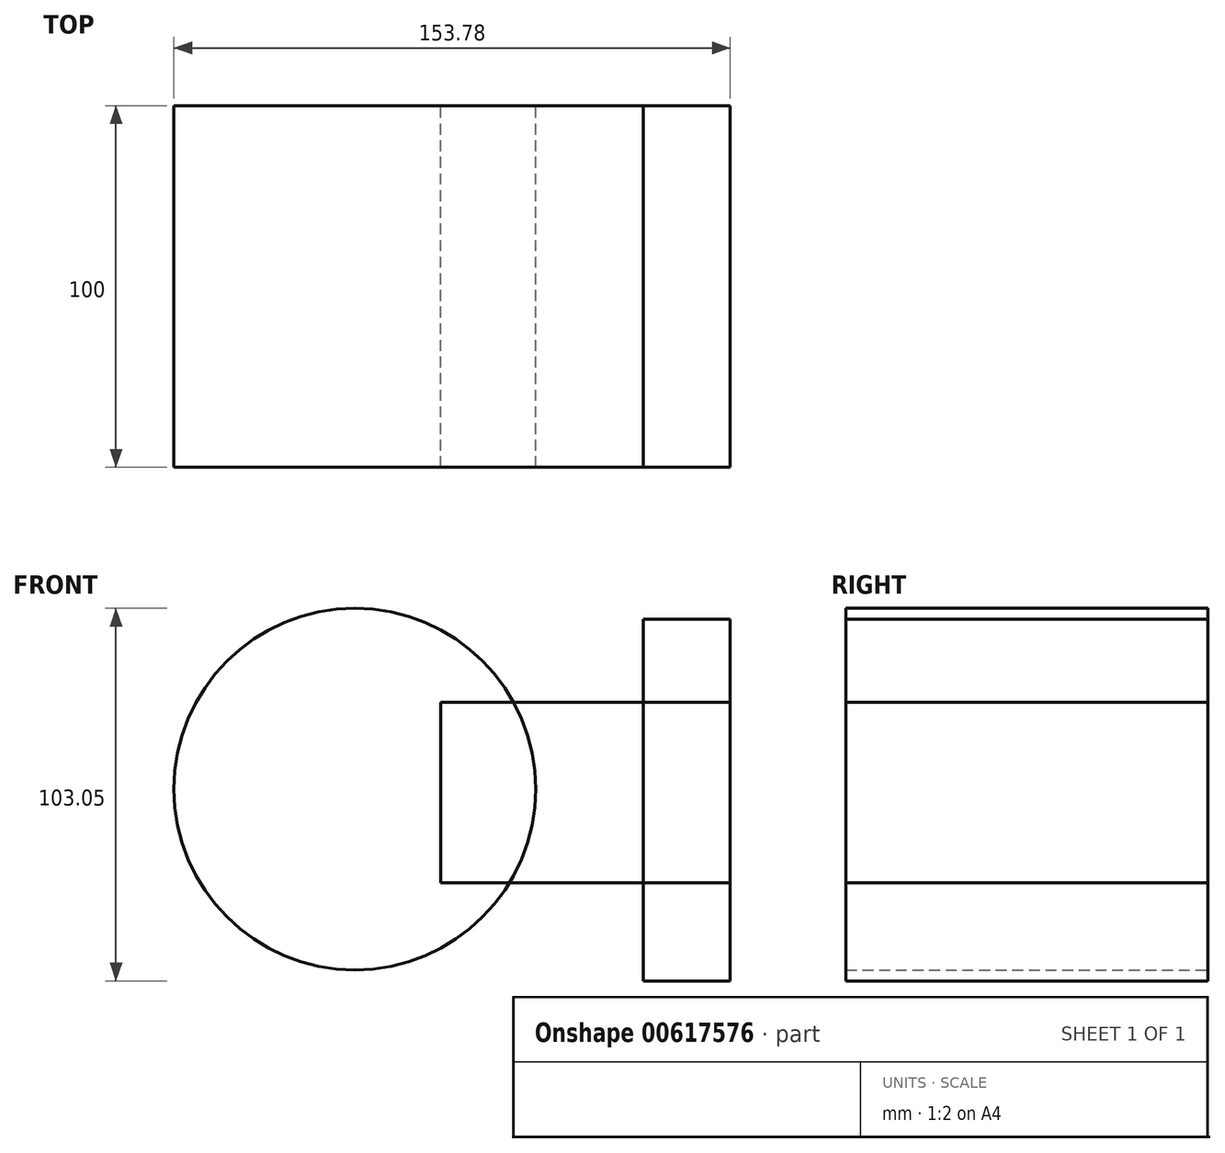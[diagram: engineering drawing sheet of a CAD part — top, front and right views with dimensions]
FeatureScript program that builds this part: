
annotation { "Feature Type Name" : "Feature", "Feature Type Description" : "" }
export const myFeature = defineFeature(function(context is Context, id is Id, definition is map)
    precondition{}
    {
        {
            var Q0;
            Q0=qCreatedBy(makeId("Front.planeOp"),FACE);
            var sketch = newSketch(context, id + "F0", { "sketchPlane" : qUnion([Q0])});
            skCircle(sketch, "E0", {"center": v(-79.77, 0) * mm, "radius": 50 * mm});
            skSolve(sketch);
        }
        {
            var Q0;
            Q0=qCreatedBy(makeId("Front.planeOp"),FACE);
            var sketch = newSketch(context, id + "F1", { "sketchPlane" : qUnion([Q0])});
            skLineSegment(sketch, "E1.bottom", {"start": v(-55.99, 24.05) * mm, "end": v(24.01, 24.05) * mm});
            skLineSegment(sketch, "E1.top", {"start": v(-55.99, -25.95) * mm, "end": v(24.01, -25.95) * mm});
            skLineSegment(sketch, "E1.left", {"start": v(-55.99, 24.05) * mm, "end": v(-55.99, -25.95) * mm});
            skLineSegment(sketch, "E1.right", {"start": v(24.01, 24.05) * mm, "end": v(24.01, -25.95) * mm});
            skSolve(sketch);
        }
        {
            var Q0;
            Q0=qCreatedBy(makeId("Front.planeOp"),FACE);
            var sketch = newSketch(context, id + "F2", { "sketchPlane" : qUnion([Q0])});
            skLineSegment(sketch, "E2.bottom", {"start": v(24, 46.95) * mm, "end": v(0, 46.95) * mm});
            skLineSegment(sketch, "E2.top", {"start": v(24, -53.05) * mm, "end": v(0, -53.05) * mm});
            skLineSegment(sketch, "E2.left", {"start": v(24, 46.95) * mm, "end": v(24, -53.05) * mm});
            skLineSegment(sketch, "E2.right", {"start": v(0, 46.95) * mm, "end": v(0, -53.05) * mm});
            skSolve(sketch);
        }
        {
            var Q0;
            Q0=makeQuery(id+"F2.imprint","IMPRINT",FACE,{"disambiguationData":[TD([[makeQuery(id+"F2.imprint","IMPRINT",EDGE,{"derivedFrom":sQuery(id+"F2.wireOp",EDGE,"E2.bottom")}),1.0]])]});
            var Q1;
            Q1=makeQuery(id+"F1.imprint","IMPRINT",FACE,{"disambiguationData":[TD([[makeQuery(id+"F1.imprint","IMPRINT",EDGE,{"derivedFrom":sQuery(id+"F1.wireOp",EDGE,"E1.bottom")}),-1.0]])]});
            var Q2;
            Q2=makeQuery(id+"F0.imprint","IMPRINT",FACE,{"disambiguationData":[TD([[makeQuery(id+"F0.imprint","IMPRINT",EDGE,{"derivedFrom":sQuery(id+"F0.wireOp",EDGE,"E0")}),1.0]])]});
            extrude(context, id + "F3", {"entities" : qUnion([Q0, Q1, Q2]), "depth" : 100 * mm, "offsetDistance" : 25 * mm});
        }
    });
